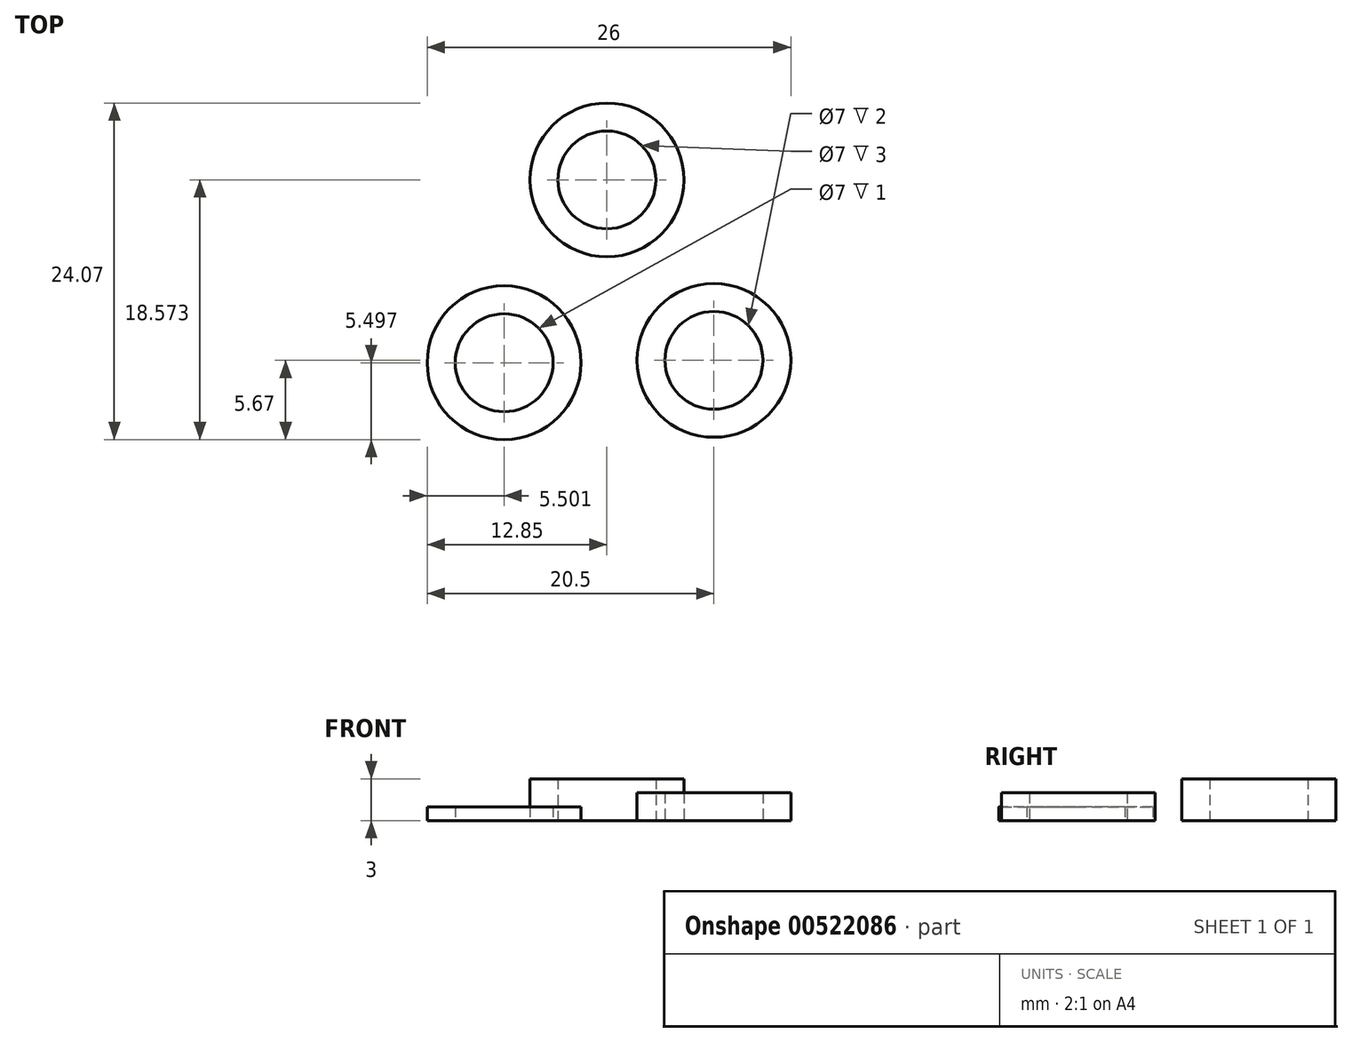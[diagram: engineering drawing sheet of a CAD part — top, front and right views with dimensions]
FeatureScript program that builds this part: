
annotation { "Feature Type Name" : "Feature", "Feature Type Description" : "" }
export const myFeature = defineFeature(function(context is Context, id is Id, definition is map)
    precondition{}
    {
        {
            var Q0;
            Q0=qCreatedBy(makeId("Top.planeOp"),FACE);
            var sketch = newSketch(context, id + "F0", { "sketchPlane" : qUnion([Q0])});
            skCircle(sketch, "E0", {"center": v(-15, 25.18) * mm, "radius": 3.5 * mm});
            skCircle(sketch, "E1", {"center": v(-15, 25.18) * mm, "radius": 5.5 * mm});
            skCircle(sketch, "E2", {"center": v(0, 25.35) * mm, "radius": 3.5 * mm});
            skCircle(sketch, "E3", {"center": v(0, 25.35) * mm, "radius": 5.5 * mm});
            skCircle(sketch, "E4", {"center": v(-7.65, 38.25) * mm, "radius": 3.5 * mm});
            skCircle(sketch, "E5", {"center": v(-7.65, 38.25) * mm, "radius": 5.5 * mm});
            skLineSegment(sketch, "E6", {"start": v(-7.65, 38.25) * mm, "end": v(-15, 25.18) * mm, "construction": true});
            skLineSegment(sketch, "E7", {"start": v(0, 25.35) * mm, "end": v(-7.65, 38.25) * mm, "construction": true});
            skLineSegment(sketch, "E8", {"start": v(-15, 25.18) * mm, "end": v(0, 25.35) * mm, "construction": true});
            skSolve(sketch);
        }
        {
            var Q0;
            Q0=makeQuery(id+"F0.imprint","IMPRINT",FACE,{"disambiguationData":[TD([[makeQuery(id+"F0.imprint","IMPRINT",EDGE,{"derivedFrom":sQuery(id+"F0.wireOp",EDGE,"E0")}),-1.0]])]});
            extrude(context, id + "F1", {"entities" : qUnion([Q0]), "depth" : 1 * mm, "offsetDistance" : 25.4 * mm});
        }
        {
            var Q0;
            Q0=makeQuery(id+"F0.imprint","IMPRINT",FACE,{"disambiguationData":[TD([[makeQuery(id+"F0.imprint","IMPRINT",EDGE,{"derivedFrom":sQuery(id+"F0.wireOp",EDGE,"E2")}),-1.0]])]});
            extrude(context, id + "F2", {"entities" : qUnion([Q0]), "depth" : 2 * mm, "offsetDistance" : 25.4 * mm});
        }
        {
            var Q0;
            Q0=makeQuery(id+"F0.imprint","IMPRINT",FACE,{"disambiguationData":[TD([[makeQuery(id+"F0.imprint","IMPRINT",EDGE,{"derivedFrom":sQuery(id+"F0.wireOp",EDGE,"E4")}),-1.0]])]});
            extrude(context, id + "F3", {"entities" : qUnion([Q0]), "depth" : 3 * mm, "offsetDistance" : 25.4 * mm});
        }
    });
